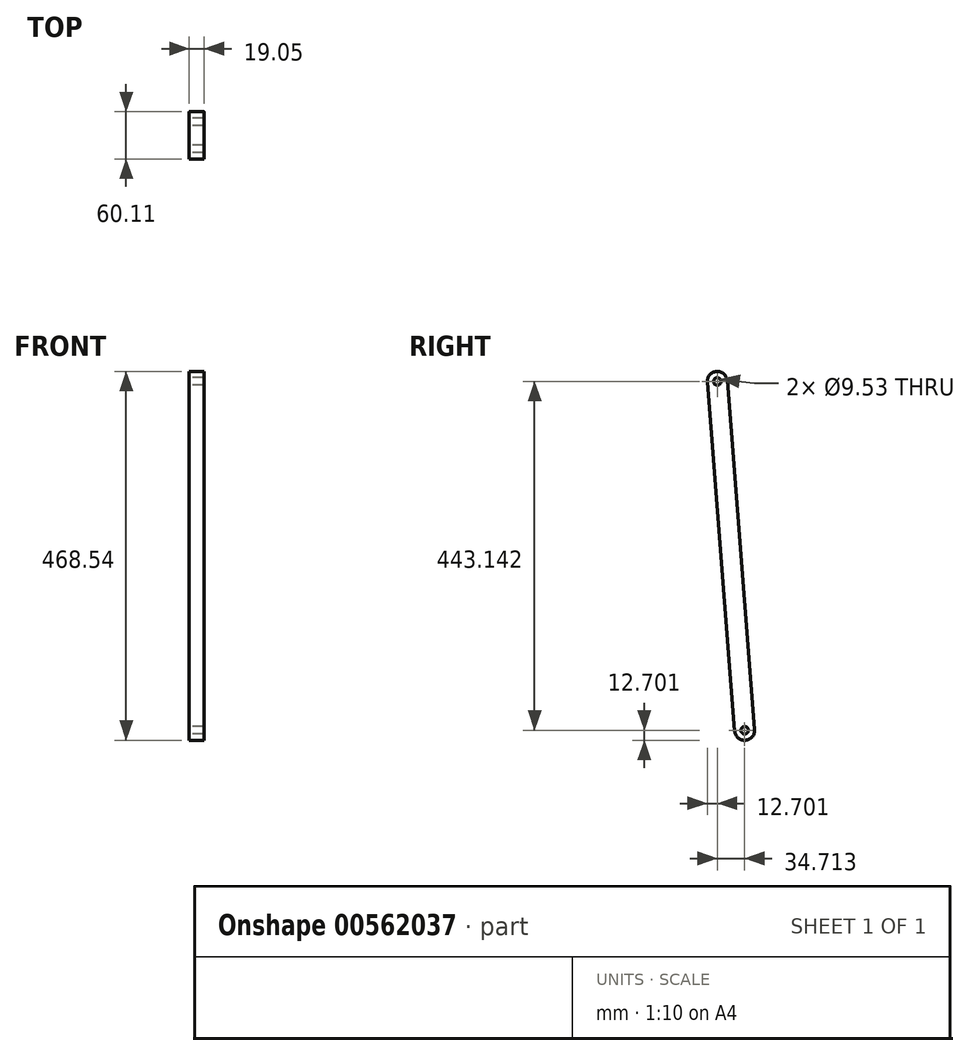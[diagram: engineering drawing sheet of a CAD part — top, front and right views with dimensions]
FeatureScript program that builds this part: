
annotation { "Feature Type Name" : "Feature", "Feature Type Description" : "" }
export const myFeature = defineFeature(function(context is Context, id is Id, definition is map)
    precondition{}
    {
        {
            var Q0;
            Q0=qCreatedBy(makeId("Right.planeOp"),FACE);
            var sketch = newSketch(context, id + "F0", { "sketchPlane" : qUnion([Q0])});
            skLineSegment(sketch, "E0", {"start": v(-513.86, 319.86) * mm, "end": v(-513.86, 78.56) * mm});
            skSolve(sketch);
        }
        {
            var Q0;
            Q0=qCreatedBy(makeId("Right.planeOp"),FACE);
            var sketch = newSketch(context, id + "F1", { "sketchPlane" : qUnion([Q0])});
            skLineSegment(sketch, "E1", {"start": v(-749.75, 255.82) * mm, "end": v(-601.81, 261.03) * mm});
            skLineSegment(sketch, "E2", {"start": v(-562.01, 653.81) * mm, "end": v(-601.81, 261.03) * mm});
            skLineSegment(sketch, "E3", {"start": v(-562.01, 653.81) * mm, "end": v(-749.75, 255.82) * mm});
            skLineSegment(sketch, "E4", {"start": v(-712.77, 291.22) * mm, "end": v(-724.6, 436.35) * mm});
            skLineSegment(sketch, "E5", {"start": v(-712.77, 291.22) * mm, "end": v(-827.72, 541.93) * mm});
            skLineSegment(sketch, "E6", {"start": v(-724.6, 436.35) * mm, "end": v(-827.72, 541.93) * mm});
            skLineSegment(sketch, "E7", {"start": v(-1010.22, 658.42) * mm, "end": v(-827.72, 541.93) * mm});
            skLineSegment(sketch, "E8", {"start": v(-1039.51, 675.34) * mm, "end": v(-1010.22, 658.42) * mm});
            skLineSegment(sketch, "E9", {"start": v(-1039.51, 675.34) * mm, "end": v(-712.77, 291.22) * mm});
            skLineSegment(sketch, "E10", {"start": v(-1010.22, 658.42) * mm, "end": v(-712.77, 291.22) * mm});
            skLineSegment(sketch, "E11", {"start": v(-601.81, 261.03) * mm, "end": v(-595.89, 401.8) * mm});
            skLineSegment(sketch, "E12", {"start": v(-601.81, 261.03) * mm, "end": v(-609.7, 655.84) * mm});
            skLineSegment(sketch, "E13", {"start": v(-595.89, 401.8) * mm, "end": v(-609.7, 655.84) * mm});
            skLineSegment(sketch, "E14", {"start": v(-724.6, 436.35) * mm, "end": v(-595.89, 401.8) * mm});
            skLineSegment(sketch, "E15", {"start": v(-827.72, 541.93) * mm, "end": v(-776.2, 589.57) * mm});
            skLineSegment(sketch, "E16", {"start": v(-749.75, 255.82) * mm, "end": v(-776.2, 589.57) * mm});
            skLineSegment(sketch, "E17", {"start": v(-1043.9, 791.38) * mm, "end": v(-776.2, 589.57) * mm});
            skLineSegment(sketch, "E18", {"start": v(-1392.46, 315.43) * mm, "end": v(-1338.48, 358.4) * mm});
            skLineSegment(sketch, "E19", {"start": v(-1338.48, 358.4) * mm, "end": v(-1296.78, 299.05) * mm});
            skLineSegment(sketch, "E20", {"start": v(-1043.9, 791.38) * mm, "end": v(-1296.78, 299.05) * mm});
            skLineSegment(sketch, "E21", {"start": v(-1296.78, 299.05) * mm, "end": v(-1039.51, 675.34) * mm});
            skLineSegment(sketch, "E22", {"start": v(-1039.51, 675.34) * mm, "end": v(-1043.9, 791.38) * mm});
            skLineSegment(sketch, "E23", {"start": v(-1010.22, 658.42) * mm, "end": v(-1338.48, 358.4) * mm});
            skLineSegment(sketch, "E24", {"start": v(-1392.46, 315.43) * mm, "end": v(-1296.78, 299.05) * mm});
            skLineSegment(sketch, "E25", {"start": v(-1296.78, 299.05) * mm, "end": v(-1296.78, 190.05) * mm});
            skLineSegment(sketch, "E26", {"start": v(-1296.78, 190.05) * mm, "end": v(-1404.89, 208.55) * mm});
            skLineSegment(sketch, "E27", {"start": v(-1404.89, 208.55) * mm, "end": v(-1392.46, 315.43) * mm});
            skLineSegment(sketch, "E28", {"start": v(-1392.46, 315.43) * mm, "end": v(-1296.78, 190.05) * mm});
            skLineSegment(sketch, "E29", {"start": v(0, 0) * mm, "end": v(0, 674.17) * mm});
            skLineSegment(sketch, "E30", {"start": v(-316.61, 320.6) * mm, "end": v(-316.61, 307.94) * mm});
            skLineSegment(sketch, "E31", {"start": v(-400.45, 218.07) * mm, "end": v(-378.01, 218.07) * mm});
            skLineSegment(sketch, "E32", {"start": v(-472.6, 74.76) * mm, "end": v(-472.6, 54.94) * mm});
            skSolve(sketch);
        }
        {
            var Q0;
            Q0=qCreatedBy(makeId("Right.planeOp"),FACE);
            var sketch = newSketch(context, id + "F2", { "sketchPlane" : qUnion([Q0])});
            skArc(sketch, "E33", {"start": v(-797.12, 697.97) * mm, "mid": v(-785.45, 711.62) * mm, "end": v(-771.8, 699.96) * mm});
            skArc(sketch, "E34", {"start": v(-762.4, 254.83) * mm, "mid": v(-748.75, 243.16) * mm, "end": v(-737.08, 256.81) * mm});
            skLineSegment(sketch, "E35", {"start": v(-762.4, 254.83) * mm, "end": v(-797.12, 697.97) * mm});
            skLineSegment(sketch, "E36", {"start": v(-771.8, 699.96) * mm, "end": v(-737.08, 256.81) * mm});
            skCircle(sketch, "E37", {"center": v(-784.46, 698.96) * mm, "radius": 4.76 * mm});
            skCircle(sketch, "E38", {"center": v(-749.75, 255.82) * mm, "radius": 4.76 * mm});
            skSolve(sketch);
        }
        {
            var Q0;
            Q0=qSketchRegion(id+"F2",true);
            extrude(context, id + "F3", {"entities" : qUnion([Q0]), "depth" : 19.05 * mm, "offsetDistance" : 25.4 * mm});
        }
    });
